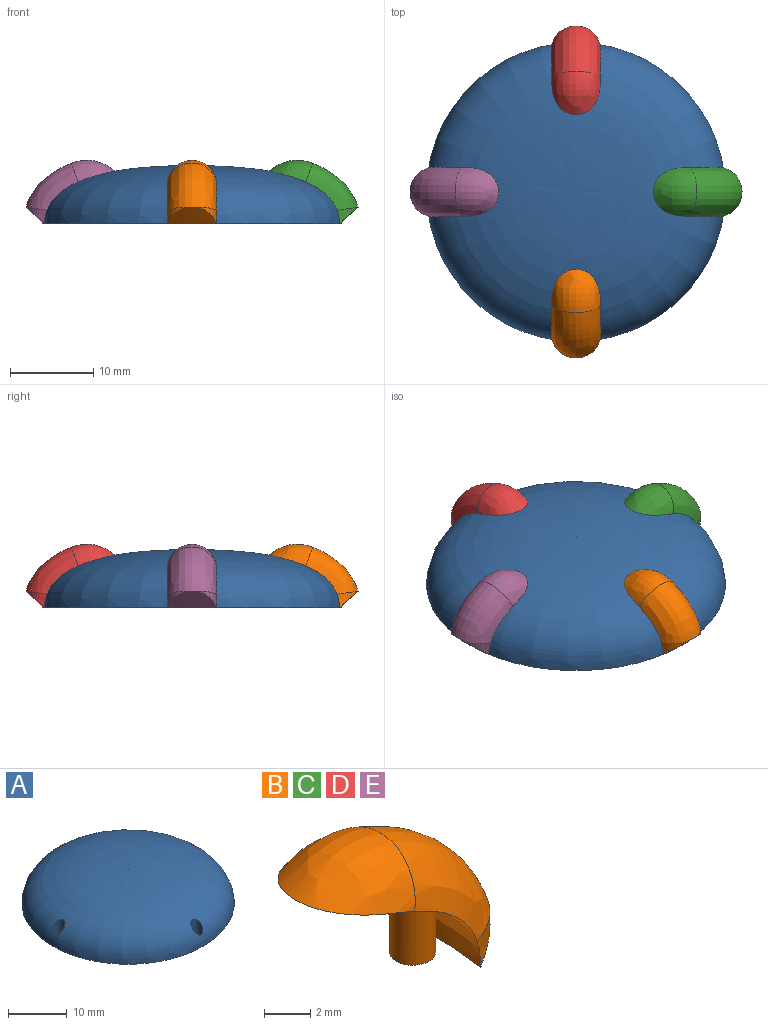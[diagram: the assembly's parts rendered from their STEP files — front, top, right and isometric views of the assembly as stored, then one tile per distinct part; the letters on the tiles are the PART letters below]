
ASSEMBLY  parts=5 mates=4
PART A: 6 faces, bbox 36x36x7 mm
  f0: revolved ~36x36mm, area -254mm2, adj f1,f2,f3,f4,f5
  f1: plane 36x36mm, normal (0,0,-1), area 1005.3mm2, adj f0,f2,f3,f4,f5
  f2: cylinder r=1mm len=4.24mm, axis (0,0,-1), area 20.8mm2, adj f0,f1
  f3: cylinder r=1mm len=4.24mm, axis (0,0,-1), area 20.8mm2, adj f0,f1
  f4: cylinder r=1mm len=4.24mm, axis (0,0,-1), area 20.8mm2, adj f0,f1
  f5: cylinder r=1mm len=4.24mm, axis (0,0,-1), area 20.8mm2, adj f0,f1
PART B: 8 faces, bbox 13.9x8.2x10.1 mm
  f0: bspline ~6x6mm, area 3.1mm2, adj f2,f4,f5
  f1: bspline ~5.88x5.15mm, area 32.6mm2, adj f2,f4
  f2: bspline ~9.5x9.31mm, area 57.9mm2, adj f0,f1,f3,f4,f5
  f3: bspline ~6x6mm, area 3.1mm2, adj f2,f4,f5
  f4: revolved ~8.94x8.19mm, area 61.1mm2, adj f0,f1,f2,f3,f5,f7
  f5: cone r=18mm half-angle=45deg, axis (0,0,1), area 12.3mm2, adj f0,f2,f3,f4
  f6: plane 2x2mm, normal (0,0,-1), area 3.1mm2, adj f7
  f7: cylinder r=1mm len=4.24mm, axis (0,0,-1), area 20.8mm2, adj f4,f6
PART C: same geometry as B
PART D: same geometry as B
PART E: same geometry as B
PLACE A t=(-10.74,-6.3,-5.82)mm
PLACE B rot(axis=(0,0,-1),90deg) t=(-10.74,-6.3,-5.82)mm
PLACE C t=(-10.74,-6.3,-5.82)mm
PLACE D rot(axis=(0,0,1),90deg) t=(-10.74,-6.3,-5.82)mm
PLACE E rot(axis=(0,0,1),180deg) t=(-10.74,-6.3,-5.82)mm
MATE fastened B.f7 <-> A.f4  axis (0,0,-1) through (-10.74,-22.8,-5.82)mm
MATE fastened C.f7 <-> A.f2  axis (0,0,-1) through (5.76,-6.3,-5.82)mm
MATE fastened E.f7 <-> A.f5  axis (0,0,-1) through (-27.24,-6.3,-5.82)mm
MATE fastened D.f7 <-> A.f3  axis (0,0,-1) through (-10.74,10.2,-5.82)mm
